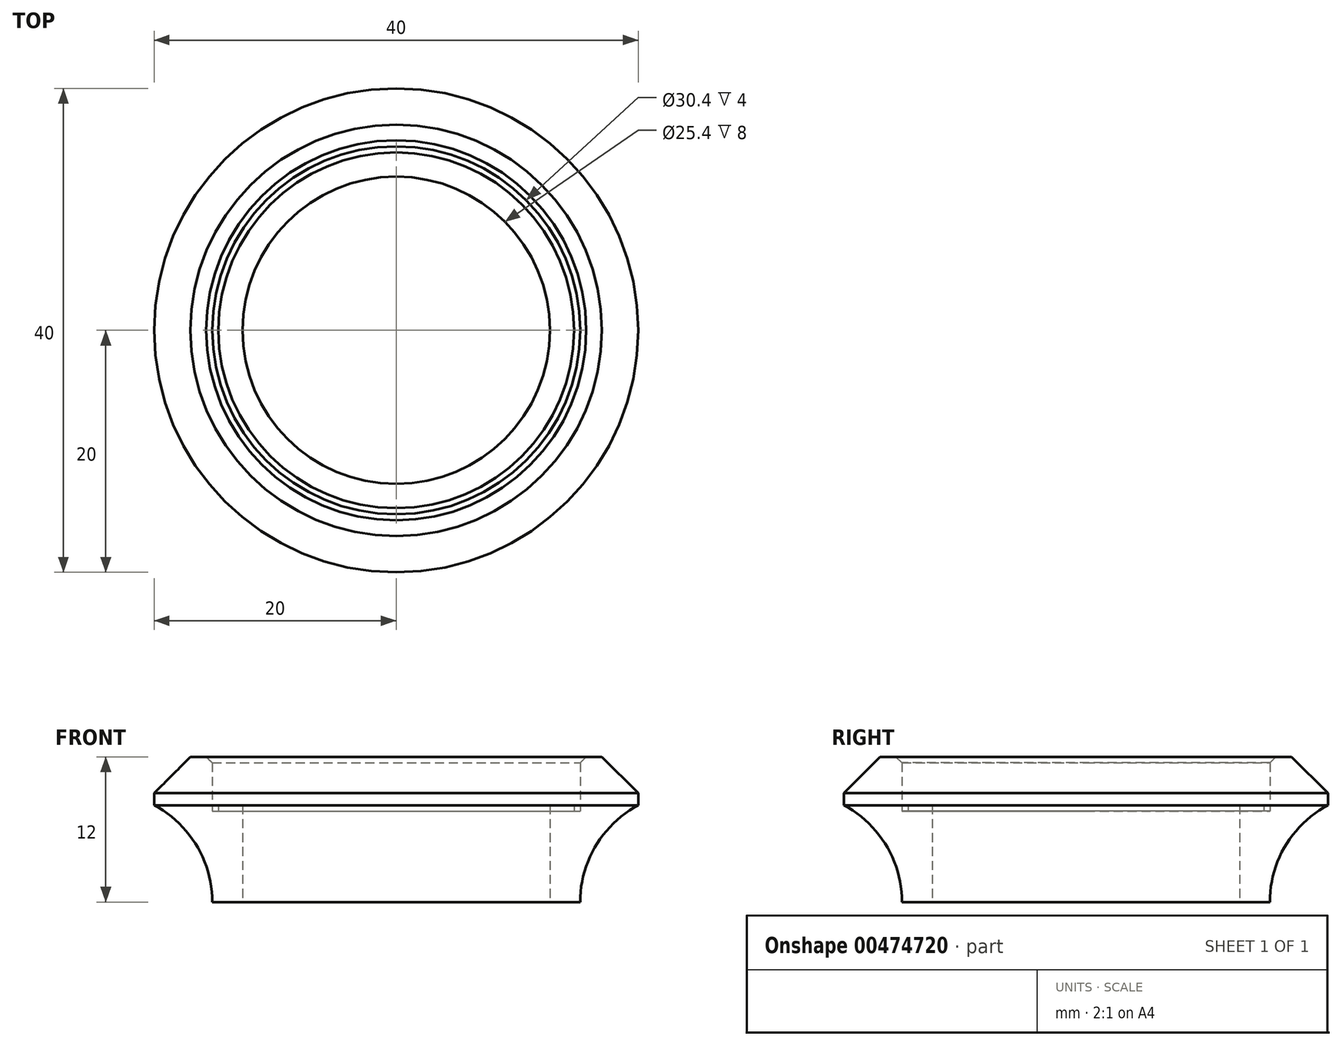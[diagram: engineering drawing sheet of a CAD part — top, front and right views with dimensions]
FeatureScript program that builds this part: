
annotation { "Feature Type Name" : "Feature", "Feature Type Description" : "" }
export const myFeature = defineFeature(function(context is Context, id is Id, definition is map)
    precondition{}
    {
        {
            var Q0;
            Q0=qCreatedBy(makeId("Front.planeOp"),FACE);
            var sketch = newSketch(context, id + "F0", { "sketchPlane" : qUnion([Q0])});
            skLineSegment(sketch, "E0", {"start": v(0, 0) * mm, "end": v(0, 12) * mm, "construction": true});
            skLineSegment(sketch, "E1", {"start": v(12.7, 0) * mm, "end": v(12.7, 8) * mm});
            skLineSegment(sketch, "E2", {"start": v(12.7, 8) * mm, "end": v(14.7, 8) * mm});
            skLineSegment(sketch, "E3", {"start": v(15.2, 7.5) * mm, "end": v(15.2, 12) * mm});
            skLineSegment(sketch, "E4", {"start": v(15.2, 12) * mm, "end": v(17, 12) * mm});
            skLineSegment(sketch, "E5", {"start": v(17, 12) * mm, "end": v(20, 9) * mm});
            skLineSegment(sketch, "E6", {"start": v(20, 9) * mm, "end": v(20, 8) * mm});
            skArc(sketch, "E7", {"start": v(20, 8) * mm, "mid": v(16.5, 4.66) * mm, "end": v(15.2, 0) * mm});
            skLineSegment(sketch, "E8", {"start": v(12.7, 0) * mm, "end": v(15.2, 0) * mm});
            skLineSegment(sketch, "E9", {"start": v(15.2, 0) * mm, "end": v(15.2, 7.5) * mm, "construction": true});
            skLineSegment(sketch, "E10", {"start": v(14.7, 8) * mm, "end": v(14.7, 7.5) * mm});
            skLineSegment(sketch, "E11", {"start": v(14.7, 7.5) * mm, "end": v(15.2, 7.5) * mm});
            skSolve(sketch);
        }
        {
            var Q0;
            Q0 = qSketchRegion(id + "F0", true);
            var Q1;
            Q1=sQuery(id+"F0.wireOp",EDGE,"E0");
            revolve(context, id + "F1", {"surfaceOperationType" : NewSurfaceOperationType.NEW, "entities" : qUnion([Q0]), "axis" : qUnion([Q1]), "revolveType" : RevolveType.FULL});
        }
        {
            var Q0;
            Q0=makeQuery(id+"F1.opRevolve","SWEPT_EDGE",EDGE,{"disambiguationData":[OSD([sQuery(id+"F0.wireOp",EDGE,"E3"),sQuery(id+"F0.wireOp",EDGE,"E4")])]});
            chamfer(context, id + "F2", {"entities" : qUnion([Q0]), "width" : 0.5 * mm, "tangentPropagation" : true});
        }
    });
